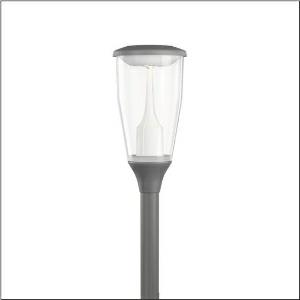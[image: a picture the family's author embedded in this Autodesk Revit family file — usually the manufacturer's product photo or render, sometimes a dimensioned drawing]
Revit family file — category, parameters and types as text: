
# Revit family: dl_11_iq___st1_2a_5xa5575af14h000022_aeb9
name_source: partatom
category: Lighting Fixtures
units: mm (PartAtom-declared; Revit-internal decimal feet)

## family parameters
Cut with Voids When Loaded = No
Host = Face
Light Source = No
Part Type = Normal
Room Calculation Point = No
Round Connector Dimension = Use Diameter
Shared = No

## types (1)
- --- (1 x LED, 1560 lm, 12.9 W, 2200K)
    Apparent Load = 13 VA
    CIE Flux Codes = 24 63 94 96 100
    Color Rendering = 70
    Color Temperature = 2200K
    Default Elevation = 1800 mm
    Description = DL 11 iQ, mast luminaire, Module 540 iQ-SR, primary light control with 3 zone facetted reflector, of plastic, silver coated, highly specular, structured, primary optical cover: cover, of PMMA, transparent, light distribution: ST1.2a, light emission: direct distribution, primary light characteristic: asymmetric, installation type: post-top, LED, High Power LED, rated luminous flux: 1.560lm, luminous efficacy: 149lm/W, light colour: 722, colour temperature: 2200K, control gear: iQ Street-Remote, control: Street-Remote, Auto-Match, Temp-Guard, Lumen-Switch, Night-Set, Smart-Wire, Light-Fading, Desk-Remote (wireless, voltage-free reading and setting of iQ features in the workshop via application-optimized NFC function/RFID function), optimised constant luminous flux control (CLO 2.0), mains connection: 220..240V, AC, 50/60Hz, connection cable pre-assembled, cable length: 5,5m, wiring characteristics: H07RN-F, 5-core, 1.5mm², start of lifetime: 13W, end of service life: 13W, reduction: 5W, luminaire housing, upper part, of diecast aluminium, coated, Siteco® metallic grey (DB 702S), spigot size: 76mm (post-top), mounting height: 3..5m, post-top mast mounting element, of diecast aluminium, coated, Siteco® metallic grey (DB 702S), Module 540 iQ-SR, traffic white (RAL 9016), equipment: standard, protection rating (complete): IP66, insulation class (complete): insulation class II (safety insulation), certification: CE, ENEC, ENEC+, VDE, impact resistance: IK07, packaging unit: 1 piece

Light Distribution: ST1.2a
    Height = 665 mm
    Lamp = 1 x LED
    Lamp Light Flux = 1560 lm
    Lamp Power = 12.9 W
    Lamp count = 1
    Length = 334 mm
    Luminous efficacy = 121 lm/W
    Manufacturer = Siteco
    ModVariant = No
    Model = 5XA5575AF14H000022
    Number of Poles = 1
    OnlyDefault = Yes
    Power Factor = 1
    Product Name = DL 11 iQ | ST1.2a
    Product group = mast luminaire | pylon top
    ProductGroupID = 6100
    Protection Class = Protection class II
    Protection Degree = IP 66
    RLX_Detail_Level = 1
    RLX_Emergency_Light_Flux = 0 lm
    RLX_Emergency_Type = 0
    RLX_Emergency_Type_DB = No
    RlxData = <blob elided: 139249 chars, md5=953c38d4>
    Socket = socket
    Standby Power = 0 W
    System Light Flux = 1560 lm
    System Power = 13 W
    Type Comments = factory setting: luminous flux: 100 % | dim-lin: 254 | 516 mA
    Type Image = l_1258354.jpg
    URL = http://relux.com
    VarID = @adj_116521
    Voltage = 0 V
    Weight = 0.00 kg
    Width = 0 mm  [stored 0 ft]

note: [stored X ft] marks values corroborated as IEEE doubles in the binary element streams (Revit-internal decimal feet)

## geometry (parser evidence)
native form markers: Blend x4, Sweep x12
no freeform markers — native parametric forms only
